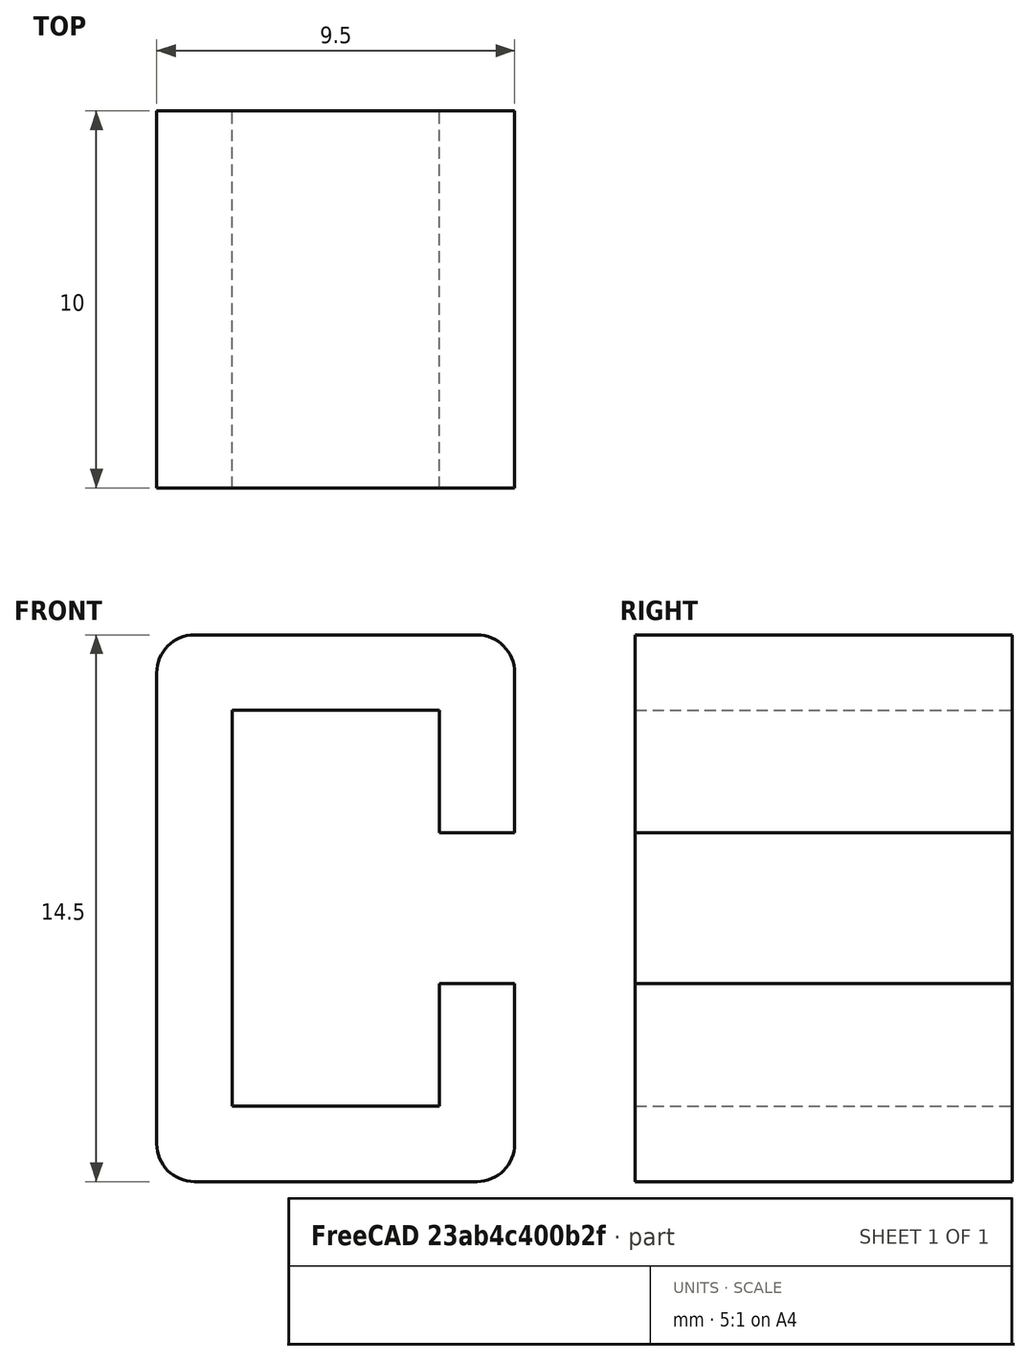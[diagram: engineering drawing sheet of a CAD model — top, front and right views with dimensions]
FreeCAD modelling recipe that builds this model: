
FCSTD DOCUMENT  (FreeCAD 0.18R16117 (Git))
Label: modified_clamp
License: All rights reserved
LicenseURL: http://en.wikipedia.org/wiki/All_rights_reserved
objects: PartDesign::Fillet×4, Mesh::Feature×3, Sketcher::SketchObject×1, PartDesign::Pad×1, PartDesign::Body×1
note: 8 computed .brp shape members not serialized (recipe doc carries the construction recipe); baked Part::Feature solids carry a one-line shape summary decoded from their .brp

FEATURE [Sketcher::SketchObject] Sketch
  AttachmentOffset = pos=(0,0,0) rot=(0.57735,-0.57735,0.57735;2.0944rad)
  Placement = pos=(-5,17.5,10) rot=(0.57735,0.57735,-0.57735;2.0944rad)
  sketch-geometry (12):
    g0: LineSegment StartX=7.25 StartY=2 StartZ=0 EndX=7.25 EndY=-7.5 EndZ=0
    g1: LineSegment StartX=7.25 StartY=-7.5 StartZ=0 EndX=-7.25 EndY=-7.5 EndZ=0
    g2: LineSegment StartX=-7.25 StartY=-7.5 StartZ=0 EndX=-7.25 EndY=2 EndZ=0
    g3: LineSegment StartX=-7.25 StartY=2 StartZ=0 EndX=-2 EndY=2 EndZ=0
    g4: LineSegment StartX=-2 StartY=2 StartZ=0 EndX=-2 EndY=0 EndZ=0
    g5: LineSegment StartX=-2 StartY=0 StartZ=0 EndX=-5.25 EndY=0 EndZ=0
    g6: LineSegment StartX=-5.25 StartY=0 StartZ=0 EndX=-5.25 EndY=-5.5 EndZ=0
    g7: LineSegment StartX=-5.25 StartY=-5.5 StartZ=0 EndX=5.25 EndY=-5.5 EndZ=0
    g8: LineSegment StartX=5.25 StartY=-5.5 StartZ=0 EndX=5.25 EndY=0 EndZ=0
    g9: LineSegment StartX=5.25 StartY=0 StartZ=0 EndX=2 EndY=0 EndZ=0
    g10: LineSegment StartX=2 StartY=0 StartZ=0 EndX=2 EndY=2 EndZ=0
    g11: LineSegment StartX=2 StartY=2 StartZ=0 EndX=7.25 EndY=2 EndZ=0
  constraints (35):
    c: Coincident(g0,g1)
    c: Coincident(g1,g2)
    c: Horizontal(g1)
    c: Vertical(g0)
    c: Vertical(g2)
    c: Coincident(g3,g2)
    c: Horizontal(g3)
    c: Coincident(g4,g3)
    c: Vertical(g4)
    c: Coincident(g5,g4)
    c: Horizontal(g5)
    c: Vertical(g6)
    c: Horizontal(g7)
    c: Coincident(g8,g7)
    c: Vertical(g8)
    c: Horizontal(g9)
    c: Coincident(g10,g9)
    c: Vertical(g10)
    c: Coincident(g11,g0)
    c: Equal(g4,g10)
    c: Equal(g3,g11)
    c: Equal(g5,g9)
    c: Equal(g0,g2)
    c: Equal(g6,g8)
    c: Coincident(g6,g7)
    c: Coincident(g5,g6)
    c: Coincident(g11,g10)
    c: Coincident(g8,g9)
    c: DistanceX(g7,g7) = 10.5
    c: DistanceY(g6,g6) = 5.5
    c: DistanceY(g4,g4) = 2
    c: DistanceX(g2,g5) = 2
    c: DistanceY(g0,g7) = 2
    c: Symmetric(g4,g9,g-1)
    c: DistanceX(g3,g10) = 4
FEATURE [PartDesign::Pad] Pad
  Length = 10
  Length2 = 100
  Placement = pos=(-5,17.5,10) rot=(0.57735,0.57735,-0.57735;2.0944rad)
  Profile = -> Sketch
  Reversed = true
  Type = 0
FEATURE [PartDesign::Fillet] Fillet
  Base = -> Pad [Edge1]
  BaseFeature = -> Pad
  Placement = pos=(-5,17.5,10) rot=(0.57735,0.57735,-0.57735;2.0944rad)
  Radius = 1
FEATURE [PartDesign::Fillet] Fillet001
  Base = -> Fillet [Edge32]
  BaseFeature = -> Fillet
  Placement = pos=(-5,17.5,10) rot=(0.57735,0.57735,-0.57735;2.0944rad)
  Radius = 1
FEATURE [PartDesign::Fillet] Fillet002
  Base = -> Fillet001 [Edge16]
  BaseFeature = -> Fillet001
  Placement = pos=(-5,17.5,10) rot=(0.57735,0.57735,-0.57735;2.0944rad)
  Radius = 1
FEATURE [PartDesign::Fillet] Fillet003
  Base = -> Fillet002 [Edge23]
  BaseFeature = -> Fillet002
  Placement = pos=(-5,17.5,10) rot=(0.57735,0.57735,-0.57735;2.0944rad)
  Radius = 1
FEATURE [PartDesign::Body] Body
  Group = -> [Sketch,Pad,Fillet,Fillet001,Fillet002,Fillet003]
  Origin = -> Origin
  Tip = -> Fillet003
FEATURE [Mesh::Feature] Mesh  label="Body (Meshed)"
FEATURE [Mesh::Feature] clamp_frame
FEATURE [Mesh::Feature] Mesh001
